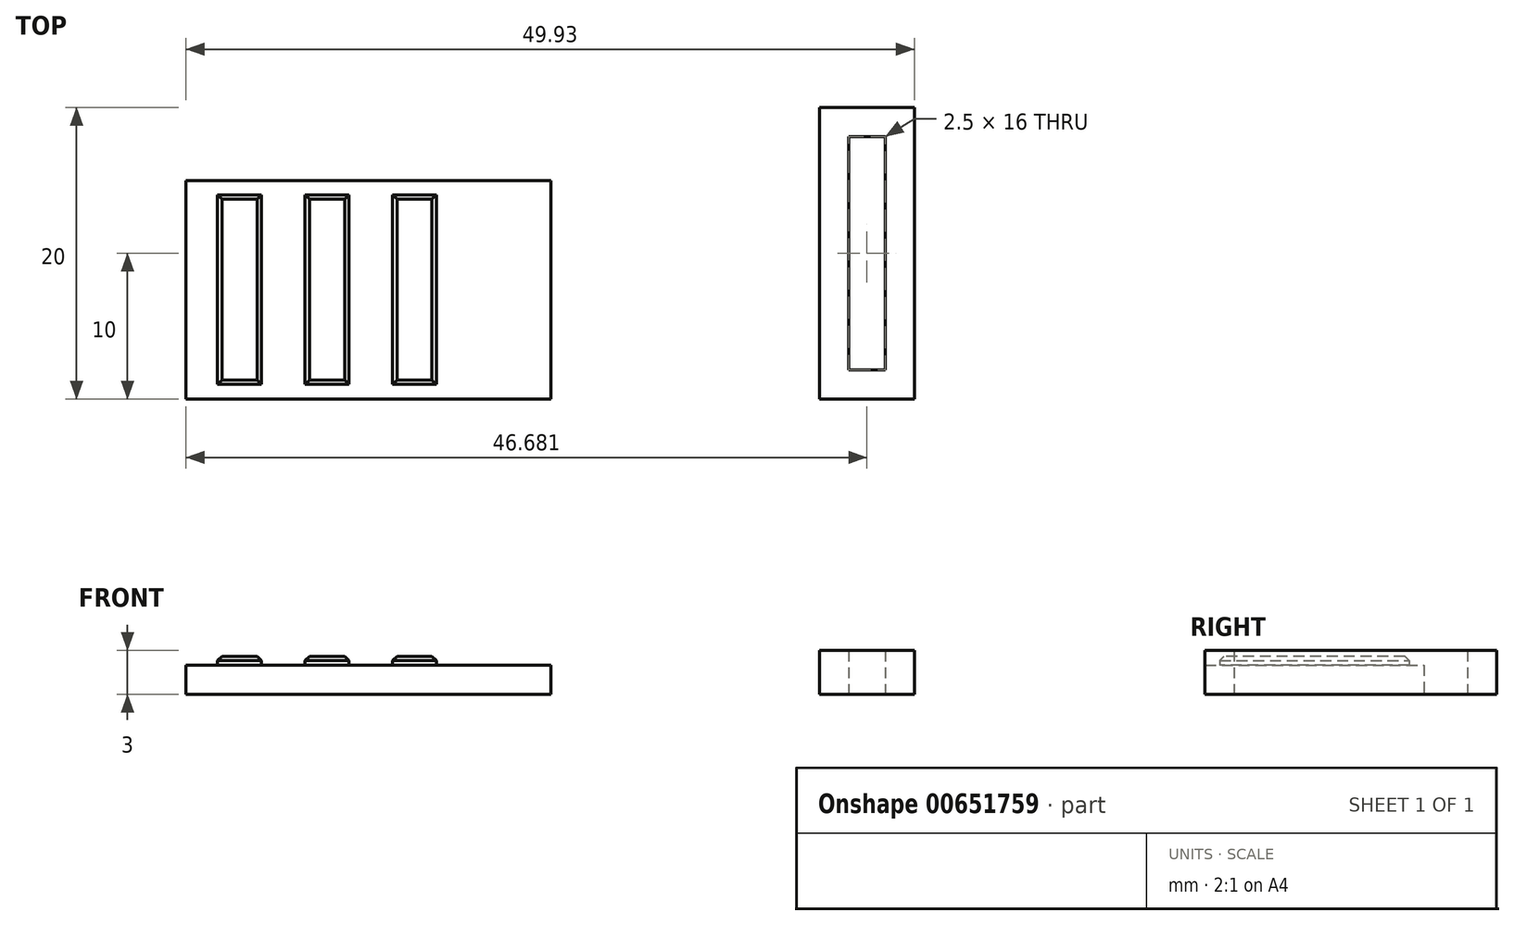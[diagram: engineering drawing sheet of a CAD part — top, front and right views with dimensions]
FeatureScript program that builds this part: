
annotation { "Feature Type Name" : "Feature", "Feature Type Description" : "" }
export const myFeature = defineFeature(function(context is Context, id is Id, definition is map)
    precondition{}
    {
        {
            var Q0;
            Q0=qCreatedBy(makeId("Top.planeOp"),FACE);
            var sketch = newSketch(context, id + "F0", { "sketchPlane" : qUnion([Q0])});
            skLineSegment(sketch, "E0.bottom", {"start": v(-6.45, 0) * mm, "end": v(-31.45, 0) * mm});
            skLineSegment(sketch, "E0.top", {"start": v(-6.45, 15) * mm, "end": v(-31.45, 15) * mm});
            skLineSegment(sketch, "E0.left", {"start": v(-6.45, 0) * mm, "end": v(-6.45, 15) * mm});
            skLineSegment(sketch, "E0.right", {"start": v(-31.45, 0) * mm, "end": v(-31.45, 15) * mm});
            skLineSegment(sketch, "E1.bottom", {"start": v(11.98, 0) * mm, "end": v(18.48, 0) * mm});
            skLineSegment(sketch, "E1.top", {"start": v(11.98, 20) * mm, "end": v(18.48, 20) * mm});
            skLineSegment(sketch, "E1.left", {"start": v(11.98, 0) * mm, "end": v(11.98, 20) * mm});
            skLineSegment(sketch, "E1.right", {"start": v(18.48, 0) * mm, "end": v(18.48, 20) * mm});
            skLineSegment(sketch, "E2.bottom", {"start": v(13.98, 18) * mm, "end": v(16.48, 18) * mm});
            skLineSegment(sketch, "E2.top", {"start": v(13.98, 2) * mm, "end": v(16.48, 2) * mm});
            skLineSegment(sketch, "E2.left", {"start": v(13.98, 18) * mm, "end": v(13.98, 2) * mm});
            skLineSegment(sketch, "E2.right", {"start": v(16.48, 18) * mm, "end": v(16.48, 2) * mm});
            skSolve(sketch);
        }
        {
            var Q0;
            Q0=makeQuery(id+"F0.imprint","IMPRINT",FACE,{"disambiguationData":[TD([[makeQuery(id+"F0.imprint","IMPRINT",EDGE,{"derivedFrom":sQuery(id+"F0.wireOp",EDGE,"E0.bottom")}),-1.0]])]});
            extrude(context, id + "F1", {"entities" : qUnion([Q0]), "depth" : 2 * mm, "offsetDistance" : 25 * mm});
        }
        {
            var Q0;
            Q0=makeQuery(id+"F0.imprint","IMPRINT",FACE,{"disambiguationData":[TD([[makeQuery(id+"F0.imprint","IMPRINT",EDGE,{"derivedFrom":sQuery(id+"F0.wireOp",EDGE,"E1.bottom")}),1.0]])]});
            extrude(context, id + "F2", {"entities" : qUnion([Q0]), "depth" : 3 * mm, "offsetDistance" : 25 * mm});
        }
        {
            var Q0;
            Q0=makeQuery(id+"F1.opExtrude","CAP_FACE",FACE,{"disambiguationData":[OSD([sQuery(id+"F0.wireOp",EDGE,"E0.bottom"),sQuery(id+"F0.wireOp",EDGE,"E0.top"),sQuery(id+"F0.wireOp",EDGE,"E0.left"),sQuery(id+"F0.wireOp",EDGE,"E0.right")])],"isStart":false});
            var sketch = newSketch(context, id + "F3", { "sketchPlane" : qUnion([Q0])});
            skLineSegment(sketch, "E3.bottom", {"start": v(-29.28, 14) * mm, "end": v(-26.28, 14) * mm});
            skLineSegment(sketch, "E3.top", {"start": v(-29.28, 1) * mm, "end": v(-26.28, 1) * mm});
            skLineSegment(sketch, "E3.left", {"start": v(-29.28, 14) * mm, "end": v(-29.28, 1) * mm});
            skLineSegment(sketch, "E3.right", {"start": v(-26.28, 14) * mm, "end": v(-26.28, 1) * mm});
            skLineSegment(sketch, "E4.bottom", {"start": v(-23.28, 14) * mm, "end": v(-20.28, 14) * mm});
            skLineSegment(sketch, "E4.top", {"start": v(-23.28, 1) * mm, "end": v(-20.28, 1) * mm});
            skLineSegment(sketch, "E4.left", {"start": v(-23.28, 14) * mm, "end": v(-23.28, 1) * mm});
            skLineSegment(sketch, "E4.right", {"start": v(-20.28, 14) * mm, "end": v(-20.28, 1) * mm});
            skLineSegment(sketch, "E5.bottom", {"start": v(-17.28, 14) * mm, "end": v(-14.28, 14) * mm});
            skLineSegment(sketch, "E5.top", {"start": v(-17.28, 1) * mm, "end": v(-14.28, 1) * mm});
            skLineSegment(sketch, "E5.left", {"start": v(-17.28, 14) * mm, "end": v(-17.28, 1) * mm});
            skLineSegment(sketch, "E5.right", {"start": v(-14.28, 14) * mm, "end": v(-14.28, 1) * mm});
            skSolve(sketch);
        }
        {
            var Q0;
            Q0=makeQuery(id+"F3.imprint","IMPRINT",FACE,{"disambiguationData":[TD([[makeQuery(id+"F3.imprint","IMPRINT",EDGE,{"derivedFrom":sQuery(id+"F3.wireOp",EDGE,"E3.bottom")}),-1.0]])]});
            var Q1;
            Q1=makeQuery(id+"F3.imprint","IMPRINT",FACE,{"disambiguationData":[TD([[makeQuery(id+"F3.imprint","IMPRINT",EDGE,{"derivedFrom":sQuery(id+"F3.wireOp",EDGE,"E4.bottom")}),-1.0]])]});
            var Q2;
            Q2=makeQuery(id+"F3.imprint","IMPRINT",FACE,{"disambiguationData":[TD([[makeQuery(id+"F3.imprint","IMPRINT",EDGE,{"derivedFrom":sQuery(id+"F3.wireOp",EDGE,"E5.bottom")}),-1.0]])]});
            extrude(context, id + "F4", {"entities" : qUnion([Q0, Q1, Q2]), "operationType" : NewBodyOperationType.ADD, "depth" : .6 * mm, "offsetDistance" : 25 * mm});
        }
        {
            var Q0;
            Q0=makeQuery(id+"F4.opExtrude","CAP_FACE",FACE,{"disambiguationData":[OSD([sQuery(id+"F3.wireOp",EDGE,"E3.bottom"),sQuery(id+"F3.wireOp",EDGE,"E3.top"),sQuery(id+"F3.wireOp",EDGE,"E3.left"),sQuery(id+"F3.wireOp",EDGE,"E3.right")])],"isStart":false});
            var Q1;
            Q1=makeQuery(id+"F4.opExtrude","CAP_FACE",FACE,{"disambiguationData":[OSD([sQuery(id+"F3.wireOp",EDGE,"E4.bottom"),sQuery(id+"F3.wireOp",EDGE,"E4.top"),sQuery(id+"F3.wireOp",EDGE,"E4.left"),sQuery(id+"F3.wireOp",EDGE,"E4.right")])],"isStart":false});
            var Q2;
            Q2=makeQuery(id+"F4.opExtrude","CAP_FACE",FACE,{"disambiguationData":[OSD([sQuery(id+"F3.wireOp",EDGE,"E5.bottom"),sQuery(id+"F3.wireOp",EDGE,"E5.top"),sQuery(id+"F3.wireOp",EDGE,"E5.left"),sQuery(id+"F3.wireOp",EDGE,"E5.right")])],"isStart":false});
            chamfer(context, id + "F5", {"entities" : qUnion([Q0, Q1, Q2]), "width" : .3 * mm, "tangentPropagation" : true});
        }
    });
